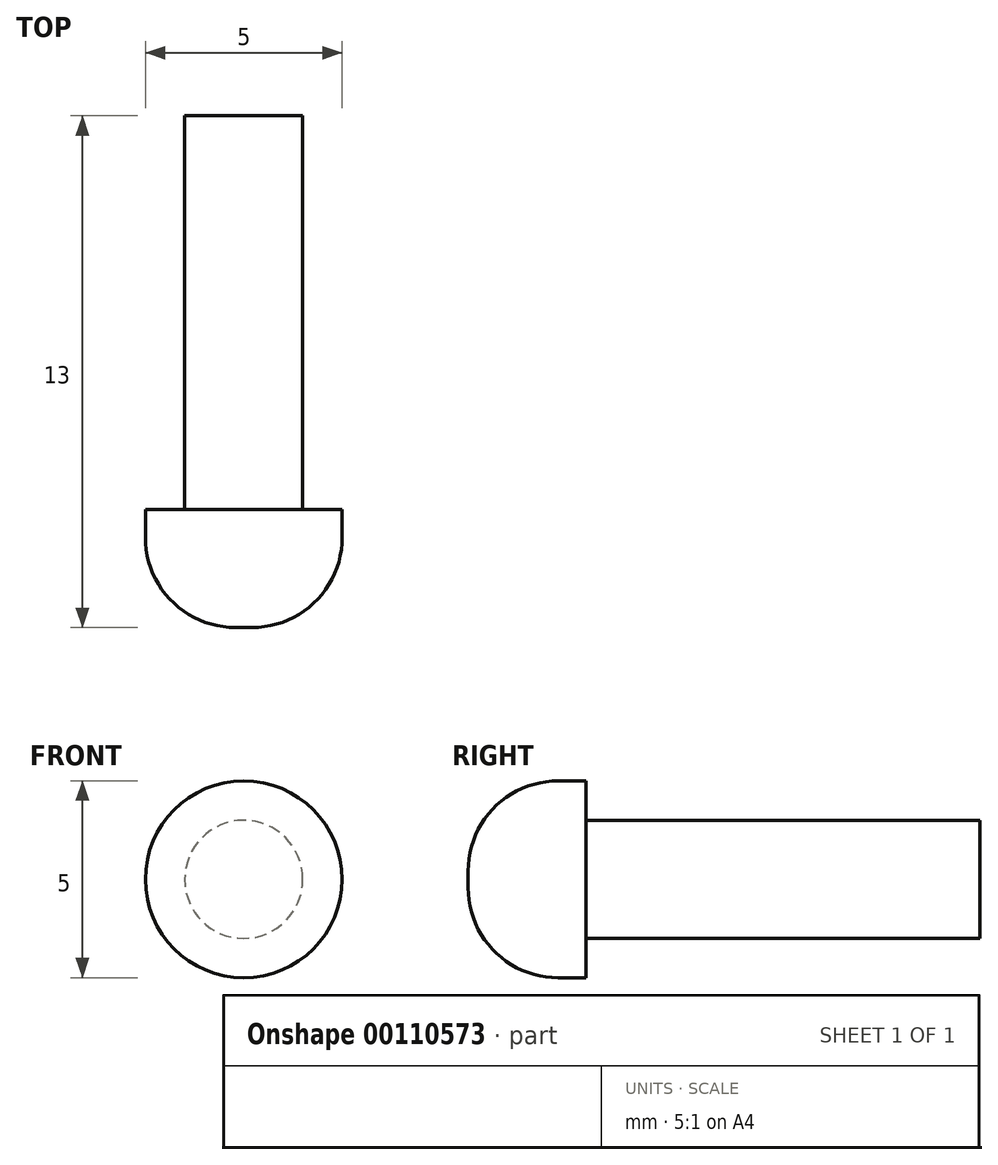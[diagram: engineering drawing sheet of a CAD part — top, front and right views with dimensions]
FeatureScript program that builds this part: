
annotation { "Feature Type Name" : "Feature", "Feature Type Description" : "" }
export const myFeature = defineFeature(function(context is Context, id is Id, definition is map)
    precondition{}
    {
        {
            var Q0;
            Q0=qCreatedBy(makeId("Front.planeOp"),FACE);
            var sketch = newSketch(context, id + "F0", { "sketchPlane" : qUnion([Q0])});
            skCircle(sketch, "E0", {"center": v(0, 0) * mm, "radius": 2.5 * mm});
            skSolve(sketch);
        }
        {
            var Q0;
            Q0 = qSketchRegion(id + "F0", true);
            var Q1;
            Q1=makeQuery(id+"F0.imprint","IMPRINT",FACE,{"disambiguationData":[TD([[makeQuery(id+"F0.imprint","IMPRINT",EDGE,{"derivedFrom":sQuery(id+"F0.wireOp",EDGE,"E0")}),1.0]])]});
            extrude(context, id + "F1", {"entities" : qUnion([Q0, Q1]), "depth" : 3 * mm});
        }
        {
            var Q0;
            Q0=makeQuery(id+"F1.opExtrude","CAP_FACE",FACE,{"disambiguationData":[OSD([sQuery(id+"F0.wireOp",EDGE,"E0")])],"isStart":true});
            var sketch = newSketch(context, id + "F2", { "sketchPlane" : qUnion([Q0])});
            skCircle(sketch, "E1", {"center": v(0, 0) * mm, "radius": 1.5 * mm});
            skSolve(sketch);
        }
        {
            var Q0;
            Q0=makeQuery(id+"F2.imprint","IMPRINT",FACE,{"disambiguationData":[TD([[makeQuery(id+"F2.imprint","IMPRINT",EDGE,{"derivedFrom":sQuery(id+"F2.wireOp",EDGE,"E1")}),1.0]])]});
            extrude(context, id + "F3", {"entities" : qUnion([Q0]), "operationType" : NewBodyOperationType.ADD, "depth" : 10 * mm});
        }
        {
            var Q0;
            Q0=makeQuery(id+"F1.opExtrude","CAP_EDGE",EDGE,{"disambiguationData":[OSD([sQuery(id+"F0.wireOp",EDGE,"E0")])],"isStart":false});
            fillet(context, id + "F4", {"entities" : qUnion([Q0]), "radius" : 2.3 * mm, "tangentPropagation" : true, "allowEdgeOverflow" : false});
        }
    });
